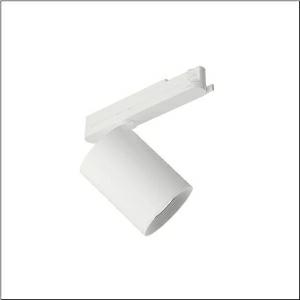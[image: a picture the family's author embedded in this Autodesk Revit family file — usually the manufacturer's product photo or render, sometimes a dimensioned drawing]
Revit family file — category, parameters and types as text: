
# Revit family: spot_21_51se13dbb5b
name_source: partatom
category: Lighting Fixtures
units: mm (PartAtom-declared; Revit-internal decimal feet)

## family parameters
Cut with Voids When Loaded = No
Host = Face
Light Source = No
Part Type = Normal
Room Calculation Point = No
Round Connector Dimension = Use Diameter
Shared = No

## types (1)
- --- (1 x LED, 5160 lm, 42.4 W, 3000K)
    Apparent Load = 42 VA
    CIE Flux Codes = 95 98 99 100 100
    Color Rendering = 90
    Color Temperature = 3000K
    Default Elevation = 1800 mm
    Description = Spot 21, directional spotlight, light control with lens, of PMMA, LED rated luminous flux: 5.120lm, light colour: 930, control gear: ECG Multilumen, with 3-phase adapter, mains connection: 220..240V, AC, 50/60Hz, of aluminium, traffic white (RAL 9016), length: 253mm, diameter: 105mm, protection rating (complete): IP20, insulation class (complete): insulation class I (protective earthing), certification: CE, impact resistance: IK02, permissible ambient temperature for indoor applications: -20..+40°C, packaging unit: 1 piece
    Height = 175 mm
    Lamp = 1 x LED
    Lamp Light Flux = 5160 lm
    Lamp Power = 42.4 W
    Lamp count = 1
    Length = 105 mm
    Luminous efficacy = 122 lm/W
    Manufacturer = Siteco
    ModVariant = No
    Model = 51SE13DBB5B
    Mounting Place = Ceiling
    Mounting Type = Pendant
    Number of Poles = 1
    OnlyDefault = Yes
    Power Factor = 1
    Product Name = Spot 21
    Product group = directional spotlight
    ProductGroupID = 906
    Protection Class = Protection class I
    Protection Degree = IP 20
    RLX_Detail_Level = 1
    RLX_Emergency_Light_Flux = 0 lm
    RLX_Emergency_Type = 0
    RLX_Emergency_Type_DB = No
    RlxData = <blob elided: 17669 chars, md5=a6c58967>
    Socket = socket
    Standby Power = 0 W
    System Light Flux = 5160 lm
    System Power = 42 W
    Type Comments = factory setting: luminous flux: 100 % | (ON | ON | ON | ON) | 1050 mA
    Type Image = l_1003976.jpg
    URL = http://relux.com
    VarID = @adj_144122
    Voltage = 0 V
    Weight = 0.00 kg
    Width = 0 mm  [stored 0 ft]

note: [stored X ft] marks values corroborated as IEEE doubles in the binary element streams (Revit-internal decimal feet)

## geometry (parser evidence)
native form markers: Blend x4, Sweep x9
no freeform markers — native parametric forms only
